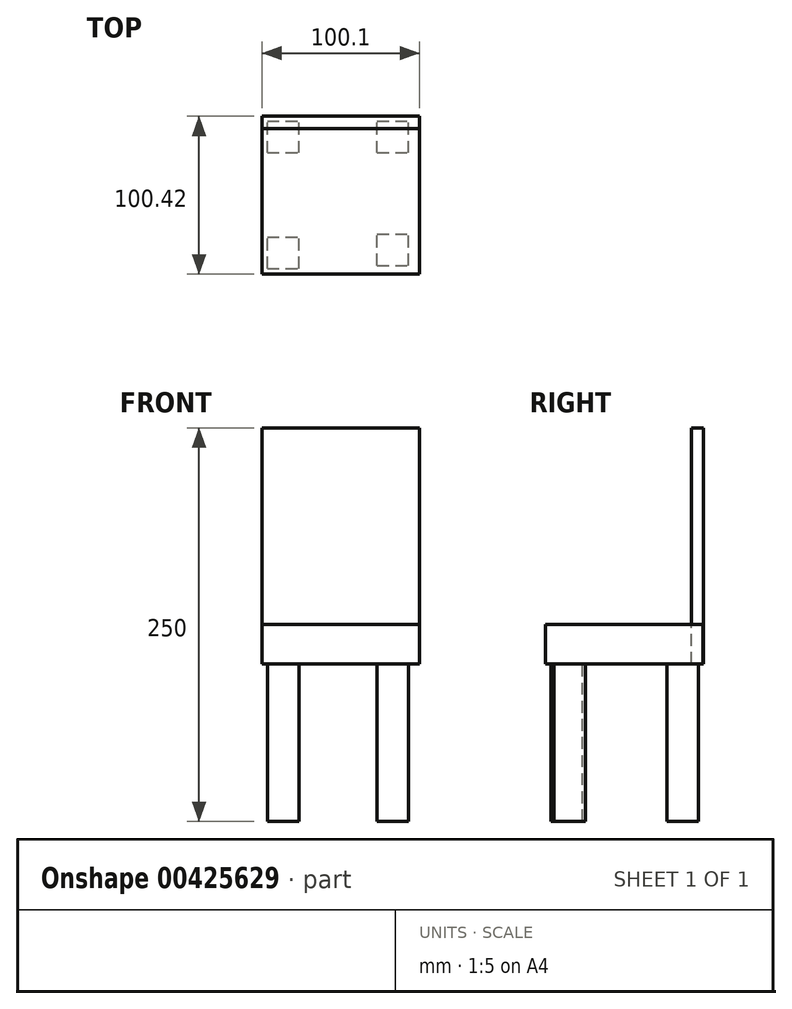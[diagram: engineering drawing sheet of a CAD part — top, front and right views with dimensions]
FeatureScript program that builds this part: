
annotation { "Feature Type Name" : "Feature", "Feature Type Description" : "" }
export const myFeature = defineFeature(function(context is Context, id is Id, definition is map)
    precondition{}
    {
        {
            var Q0;
            Q0=qCreatedBy(makeId("Top.planeOp"),FACE);
            var sketch = newSketch(context, id + "F0", { "sketchPlane" : qUnion([Q0])});
            skLineSegment(sketch, "E0.bottom", {"start": v(-49.35, 47.32) * mm, "end": v(50.65, 47.32) * mm});
            skLineSegment(sketch, "E0.top", {"start": v(-49.35, -52.68) * mm, "end": v(50.65, -52.68) * mm});
            skLineSegment(sketch, "E0.left", {"start": v(-49.35, 47.32) * mm, "end": v(-49.35, -52.68) * mm});
            skLineSegment(sketch, "E0.right", {"start": v(50.65, 47.32) * mm, "end": v(50.65, -52.68) * mm});
            skSolve(sketch);
        }
        {
            var Q0;
            Q0=makeQuery(id+"F0.imprint","IMPRINT",FACE,{"disambiguationData":[TD([[makeQuery(id+"F0.imprint","IMPRINT",EDGE,{"derivedFrom":sQuery(id+"F0.wireOp",EDGE,"E0.bottom")}),-1.0]])]});
            extrude(context, id + "F1", {"entities" : qUnion([Q0]), "depth" : 25 * mm, "offsetDistance" : 25 * mm});
        }
        {
            var Q0;
            Q0=qCreatedBy(makeId("Top.planeOp"),FACE);
            var sketch = newSketch(context, id + "F2", { "sketchPlane" : qUnion([Q0])});
            skLineSegment(sketch, "E1.bottom", {"start": v(-45.95, -49.09) * mm, "end": v(-25.95, -49.09) * mm});
            skLineSegment(sketch, "E1.top", {"start": v(-45.95, -29.09) * mm, "end": v(-25.95, -29.09) * mm});
            skLineSegment(sketch, "E1.left", {"start": v(-45.95, -49.09) * mm, "end": v(-45.95, -29.09) * mm});
            skLineSegment(sketch, "E1.right", {"start": v(-25.95, -49.09) * mm, "end": v(-25.95, -29.09) * mm});
            skLineSegment(sketch, "E2.bottom", {"start": v(23.8, -47.15) * mm, "end": v(43.8, -47.15) * mm});
            skLineSegment(sketch, "E2.top", {"start": v(23.8, -27.15) * mm, "end": v(43.8, -27.15) * mm});
            skLineSegment(sketch, "E2.left", {"start": v(23.8, -47.15) * mm, "end": v(23.8, -27.15) * mm});
            skLineSegment(sketch, "E2.right", {"start": v(43.8, -47.15) * mm, "end": v(43.8, -27.15) * mm});
            skLineSegment(sketch, "E3.bottom", {"start": v(-45.95, 24.54) * mm, "end": v(-25.95, 24.54) * mm});
            skLineSegment(sketch, "E3.top", {"start": v(-45.95, 44.54) * mm, "end": v(-25.95, 44.54) * mm});
            skLineSegment(sketch, "E3.left", {"start": v(-45.95, 24.54) * mm, "end": v(-45.95, 44.54) * mm});
            skLineSegment(sketch, "E3.right", {"start": v(-25.95, 24.54) * mm, "end": v(-25.95, 44.54) * mm});
            skLineSegment(sketch, "E4.bottom", {"start": v(23.8, 24.54) * mm, "end": v(43.8, 24.54) * mm});
            skLineSegment(sketch, "E4.top", {"start": v(23.8, 44.54) * mm, "end": v(43.8, 44.54) * mm});
            skLineSegment(sketch, "E4.left", {"start": v(23.8, 24.54) * mm, "end": v(23.8, 44.54) * mm});
            skLineSegment(sketch, "E4.right", {"start": v(43.8, 24.54) * mm, "end": v(43.8, 44.54) * mm});
            skSolve(sketch);
        }
        {
            var Q0;
            Q0=makeQuery(id+"F2.imprint","IMPRINT",FACE,{"disambiguationData":[TD([[makeQuery(id+"F2.imprint","IMPRINT",EDGE,{"derivedFrom":sQuery(id+"F2.wireOp",EDGE,"E4.bottom")}),1.0]])]});
            var Q1;
            Q1=makeQuery(id+"F2.imprint","IMPRINT",FACE,{"disambiguationData":[TD([[makeQuery(id+"F2.imprint","IMPRINT",EDGE,{"derivedFrom":sQuery(id+"F2.wireOp",EDGE,"E2.bottom")}),1.0]])]});
            var Q2;
            Q2=makeQuery(id+"F2.imprint","IMPRINT",FACE,{"disambiguationData":[TD([[makeQuery(id+"F2.imprint","IMPRINT",EDGE,{"derivedFrom":sQuery(id+"F2.wireOp",EDGE,"E3.bottom")}),1.0]])]});
            var Q3;
            Q3=makeQuery(id+"F2.imprint","IMPRINT",FACE,{"disambiguationData":[TD([[makeQuery(id+"F2.imprint","IMPRINT",EDGE,{"derivedFrom":sQuery(id+"F2.wireOp",EDGE,"E1.bottom")}),1.0]])]});
            extrude(context, id + "F3", {"entities" : qUnion([Q0, Q1, Q2, Q3]), "operationType" : NewBodyOperationType.ADD, "oppositeDirection" : true, "depth" : 100 * mm, "offsetDistance" : 25 * mm});
        }
        {
            var Q0;
            Q0=qCreatedBy(makeId("Top.planeOp"),FACE);
            var sketch = newSketch(context, id + "F4", { "sketchPlane" : qUnion([Q0])});
            skLineSegment(sketch, "E5.bottom", {"start": v(-49.45, 47.74) * mm, "end": v(50.55, 47.74) * mm});
            skLineSegment(sketch, "E5.top", {"start": v(-49.45, 39.92) * mm, "end": v(50.55, 39.92) * mm});
            skLineSegment(sketch, "E5.left", {"start": v(-49.45, 47.74) * mm, "end": v(-49.45, 39.92) * mm});
            skLineSegment(sketch, "E5.right", {"start": v(50.55, 47.74) * mm, "end": v(50.55, 39.92) * mm});
            skSolve(sketch);
        }
        {
            var Q0;
            Q0=makeQuery(id+"F4.imprint","IMPRINT",FACE,{"disambiguationData":[TD([[makeQuery(id+"F4.imprint","IMPRINT",EDGE,{"derivedFrom":sQuery(id+"F4.wireOp",EDGE,"E5.bottom")}),-1.0]])]});
            extrude(context, id + "F5", {"entities" : qUnion([Q0]), "operationType" : NewBodyOperationType.ADD, "depth" : 150 * mm, "offsetDistance" : 25 * mm});
        }
    });
